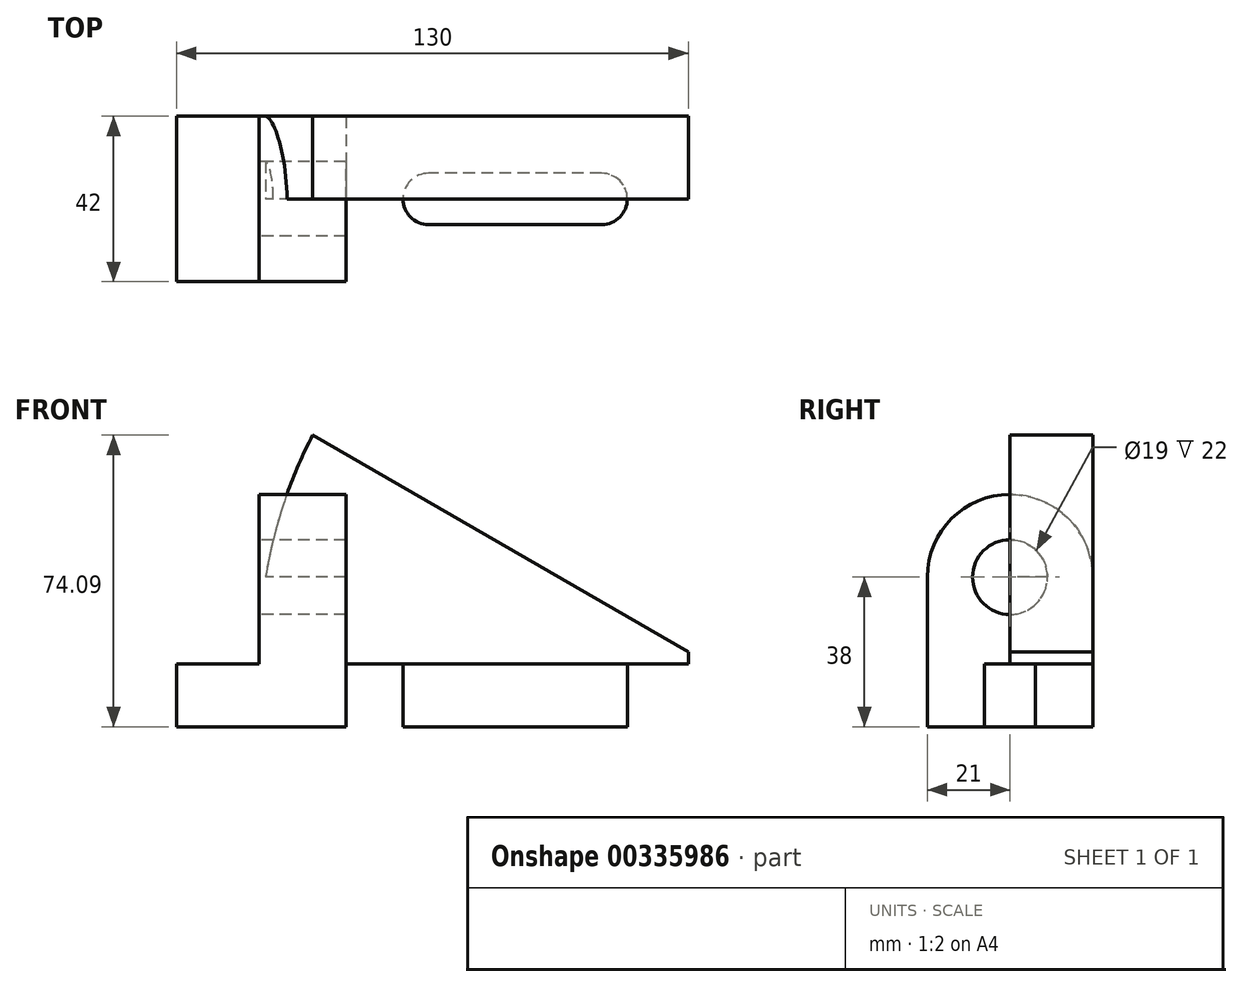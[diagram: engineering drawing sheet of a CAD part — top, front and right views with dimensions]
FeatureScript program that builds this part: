
annotation { "Feature Type Name" : "Feature", "Feature Type Description" : "" }
export const myFeature = defineFeature(function(context is Context, id is Id, definition is map)
    precondition{}
    {
        {
            var Q0;
            Q0=qCreatedBy(makeId("Right.planeOp"),FACE);
            var sketch = newSketch(context, id + "F0", { "sketchPlane" : qUnion([Q0])});
            skLineSegment(sketch, "E0", {"start": v(0, 0) * mm, "end": v(42, 0) * mm});
            skLineSegment(sketch, "E1", {"start": v(42, 0) * mm, "end": v(42, 16) * mm});
            skLineSegment(sketch, "E2", {"start": v(42, 16) * mm, "end": v(0, 16) * mm});
            skLineSegment(sketch, "E3", {"start": v(0, 16) * mm, "end": v(0, 0) * mm});
            skLineSegment(sketch, "E4", {"start": v(0, 16) * mm, "end": v(21, 16) * mm, "construction": true});
            skLineSegment(sketch, "E5", {"start": v(21, 16) * mm, "end": v(21, 38) * mm, "construction": true});
            skCircle(sketch, "E6", {"center": v(21, 38) * mm, "radius": 9.5 * mm});
            skArc(sketch, "E7", {"start": v(42, 38) * mm, "mid": v(21, 59) * mm, "end": v(0, 38) * mm});
            skLineSegment(sketch, "E8", {"start": v(0, 38) * mm, "end": v(0, 16) * mm});
            skLineSegment(sketch, "E9", {"start": v(42, 38) * mm, "end": v(42, 16) * mm});
            skSolve(sketch);
        }
        {
            var Q0;
            Q0=makeQuery(id+"F0.imprint","IMPRINT",FACE,{"disambiguationData":[TD([[makeQuery(id+"F0.imprint","IMPRINT",EDGE,{"derivedFrom":sQuery(id+"F0.wireOp",EDGE,"E0")}),1.0]])]});
            extrude(context, id + "F1", {"entities" : qUnion([Q0]), "depth" : 133 * mm});
        }
        {
            var Q0;
            Q0=makeQuery(id+"F0.imprint","IMPRINT",FACE,{"disambiguationData":[TD([[makeQuery(id+"F0.imprint","IMPRINT",EDGE,{"derivedFrom":sQuery(id+"F0.wireOp",EDGE,"E2")}),-1.0]])]});
            extrude(context, id + "F2", {"entities" : qUnion([Q0]), "operationType" : NewBodyOperationType.ADD, "depth" : 43 * mm, "hasSecondDirection" : true, "secondDirectionOppositeDirection" : false, "secondDirectionDepth" : 21 * mm});
        }
        {
            var Q0;
            {var subQ0=sQuery(id+"F0.wireOp",EDGE,"E3");var subQ3=sQuery(id+"F0.wireOp",EDGE,"E2");var subQ4=sQuery(id+"F0.wireOp",EDGE,"E1");Q0=makeQuery(id+"F2.boolean.opBoolean","SPLIT",FACE,{"disambiguationData":[TD([makeQuery(id+"F1.opExtrude","CAP_FACE",FACE,{"disambiguationData":[OSD([sQuery(id+"F0.wireOp",EDGE,"E0"),subQ4,subQ3,subQ0])],"isStart":false})])],"derivedFrom":makeQuery(id+"F1.opExtrude","SWEPT_FACE",FACE,{"disambiguationData":[OSD([subQ3])]})});}
            var sketch = newSketch(context, id + "F3", { "sketchPlane" : qUnion([Q0])});
            skLineSegment(sketch, "E10", {"start": v(133, 42) * mm, "end": v(108, 42) * mm, "construction": true});
            skLineSegment(sketch, "E11", {"start": v(108, 42) * mm, "end": v(108, 21) * mm, "construction": true});
            skLineSegment(sketch, "E12", {"start": v(108, 21) * mm, "end": v(64, 21) * mm, "construction": true});
            skArc(sketch, "E13.0.startCap", {"start": v(108, 27.5) * mm, "mid": v(114.5, 21) * mm, "end": v(108, 14.5) * mm});
            skArc(sketch, "E13.0.endCap", {"start": v(64, 14.5) * mm, "mid": v(57.5, 21) * mm, "end": v(64, 27.5) * mm});
            skLineSegment(sketch, "E13.0.left", {"start": v(108, 14.5) * mm, "end": v(64, 14.5) * mm});
            skLineSegment(sketch, "E13.0.right", {"start": v(108, 27.5) * mm, "end": v(64, 27.5) * mm});
            skSolve(sketch);
        }
        {
            var Q0;
            Q0=makeQuery(id+"F3.imprint","IMPRINT",FACE,{"disambiguationData":[TD([[makeQuery(id+"F3.imprint","IMPRINT",EDGE,{"derivedFrom":sQuery(id+"F3.wireOp",EDGE,"E13.0.startCap")}),-1.0]])]});
            extrude(context, id + "F4", {"entities" : qUnion([Q0]), "operationType" : NewBodyOperationType.REMOVE, "oppositeDirection" : true, "depth" : 25 * mm});
        }
        {
            var Q0;
            Q0=makeQuery(id+"F2.boolean.opBoolean","MERGE",FACE,{"derivedFrom":[makeQuery(id+"F1.opExtrude","SWEPT_FACE",FACE,{"disambiguationData":[OSD([sQuery(id+"F0.wireOp",EDGE,"E3")])]}),makeQuery(id+"F2.opExtrude","SWEPT_FACE",FACE,{"disambiguationData":[OSD([sQuery(id+"F0.wireOp",EDGE,"E8")])]})]});
            var sketch = newSketch(context, id + "F5", { "sketchPlane" : qUnion([Q0])});
            skLineSegment(sketch, "E14", {"start": v(0, 0) * mm, "end": v(130, 0) * mm, "construction": true});
            skLineSegment(sketch, "E15", {"start": v(130, 0) * mm, "end": v(130, 19) * mm});
            skLineSegment(sketch, "E16", {"start": v(130, 19) * mm, "end": v(34.59, 74.09) * mm});
            skLineSegment(sketch, "E17", {"start": v(21, 16) * mm, "end": v(130, 16) * mm});
            skArc(sketch, "E18", {"start": v(34.59, 74.09) * mm, "mid": v(24.16, 45.9) * mm, "end": v(21, 16) * mm});
            skSolve(sketch);
        }
        {
            var Q0;
            {var subQ1=sQuery(id+"F5.wireOp",EDGE,"E16");Q0=makeQuery(id+"F5.imprint","IMPRINT",FACE,{"disambiguationData":[TD([[makeQuery(id+"F5.imprint","IMPRINT",EDGE,{"derivedFrom":subQ1}),1.0]])]});}
            extrude(context, id + "F6", {"entities" : qUnion([Q0]), "operationType" : NewBodyOperationType.ADD, "oppositeDirection" : true, "depth" : 42 * mm, "hasSecondDirection" : true, "secondDirectionOppositeDirection" : true, "secondDirectionDepth" : 21 * mm});
        }
    });
